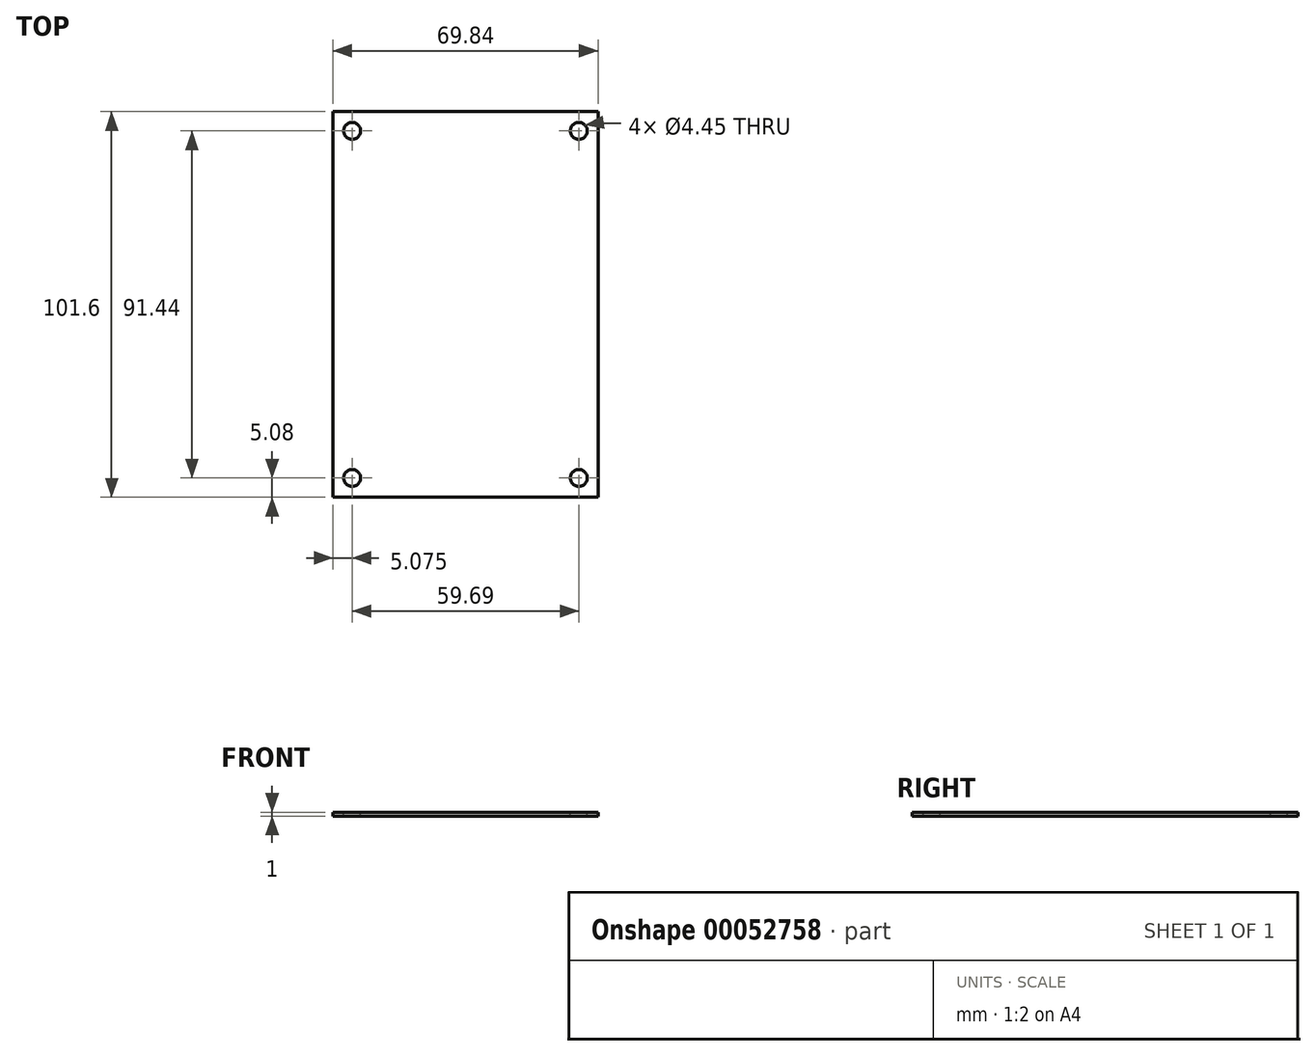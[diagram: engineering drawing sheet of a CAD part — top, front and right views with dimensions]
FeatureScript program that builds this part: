
annotation { "Feature Type Name" : "Feature", "Feature Type Description" : "" }
export const myFeature = defineFeature(function(context is Context, id is Id, definition is map)
    precondition{}
    {
        {
            var Q0;
            Q0=qCreatedBy(makeId("Top.planeOp"),FACE);
            var sketch = newSketch(context, id + "F0", { "sketchPlane" : qUnion([Q0])});
            skLineSegment(sketch, "E0.bottom", {"start": v(-34.92, 50.8) * mm, "end": v(34.93, 50.8) * mm});
            skLineSegment(sketch, "E0.top", {"start": v(-34.93, -50.8) * mm, "end": v(34.92, -50.8) * mm});
            skLineSegment(sketch, "E0.left", {"start": v(-34.92, 50.8) * mm, "end": v(-34.93, -50.8) * mm});
            skLineSegment(sketch, "E0.right", {"start": v(34.93, 50.8) * mm, "end": v(34.93, -50.8) * mm});
            skLineSegment(sketch, "E1", {"start": v(-34.92, 50.8) * mm, "end": v(34.92, -50.8) * mm, "construction": true});
            skSolve(sketch);
        }
        {
            var Q0;
            Q0 = qSketchRegion(id + "F0", true);
            extrude(context, id + "F1", {"entities" : qUnion([Q0]), "depth" : 1 * mm});
        }
        {
            var Q0;
            Q0=makeQuery(id+"F1.opExtrude","CAP_FACE",FACE,{"disambiguationData":[OSD([sQuery(id+"F0.wireOp",EDGE,"E0.bottom"),sQuery(id+"F0.wireOp",EDGE,"E0.top"),sQuery(id+"F0.wireOp",EDGE,"E0.left"),sQuery(id+"F0.wireOp",EDGE,"E0.right")])],"isStart":false});
            var sketch = newSketch(context, id + "F2", { "sketchPlane" : qUnion([Q0])});
            skCircle(sketch, "E2", {"center": v(-29.85, 45.72) * mm, "radius": 2.22 * mm});
            skCircle(sketch, "E3", {"center": v(29.85, 45.72) * mm, "radius": 2.22 * mm});
            skCircle(sketch, "E4", {"center": v(-29.85, -45.72) * mm, "radius": 2.22 * mm});
            skCircle(sketch, "E5", {"center": v(29.85, -45.72) * mm, "radius": 2.22 * mm});
            skSolve(sketch);
        }
        {
            var Q0;
            Q0 = qSketchRegion(id + "F2", true);
            extrude(context, id + "F3", {"entities" : qUnion([Q0]), "operationType" : NewBodyOperationType.REMOVE, "endBound" : BoundingType.THROUGH_ALL, "oppositeDirection" : true, "depth" : 25.4 * mm});
        }
    });
